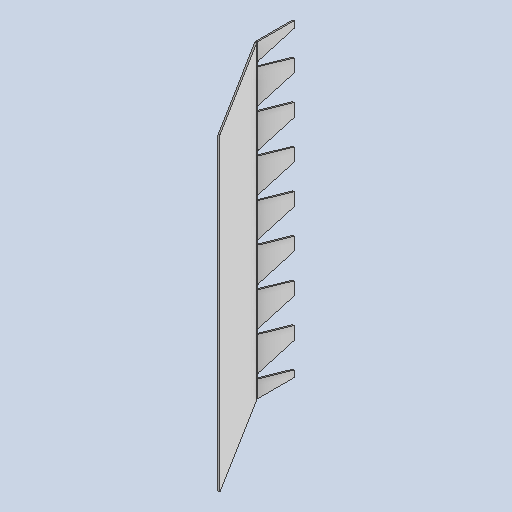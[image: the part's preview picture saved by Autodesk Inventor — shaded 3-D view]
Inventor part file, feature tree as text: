
AUTODESK INVENTOR PART (.ipt)
format: ipt  version: 2025 (Build 290162010, 162A)  size: 203,776 bytes
history: native  units: mm
features: sheet_metal_op x3, other x3, sketch x2, extrude x1, pattern_linear x1, projected_geometry x1
ambient origin geometry x8: Origin, YZ Plane, XZ Plane, XY Plane, X Axis, Y Axis, Z Axis, Center Point
bodies: Solid1 (feature_tree)
feature tree (11):
  sheet_metal_op  "Contour Flange1"
  other  "A-Side Definition"
  extrude  "Extrusion1"  Depth=5.585054mm
  pattern_linear  "Rectangular Pattern1"  Spacing1=1.0mm  [1 undecoded]
  sketch  "Sketch1"  dims[d0=950.73mm d2=5.585054mm]
  other  "Plate1"
  sheet_metal_op  "Bend1"
  sheet_metal_op  "Corner1"
  sketch  "Sketch2"  dims[d3=814.155775mm d4=1.0mm d5=10.0mm d6=10.0mm d7=5.0mm d8=20.0mm d9=10.0mm d10=2161.0mm d11=10.0mm d12=10.0mm d13=40.0mm d14=10.0mm d15=10.0mm d16=260.0mm d17=20.0mm d18=5.585054mm d19=46.0mm d20=0.0mm d21=0.0mm d22=80.0mm d24=270.0mm]
  projected_geometry  "Projected Loop1"
  other  "Definition1"
note: 1 required parameter value undecoded (feature->parameter linkage not recoverable at this tier; creation-order binding heuristic only, values carry confidence <= 0.55)
